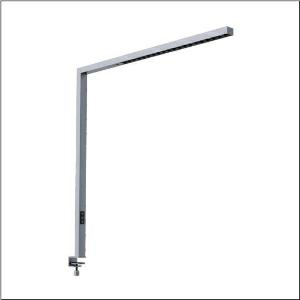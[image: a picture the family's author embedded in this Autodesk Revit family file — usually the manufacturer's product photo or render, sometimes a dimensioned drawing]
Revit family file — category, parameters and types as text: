
# Revit family: silica_r__31_desk_51my52ga3cs_3f63
name_source: partatom
category: Lighting Fixtures
units: mm (PartAtom-declared; Revit-internal decimal feet)

## family parameters
Cut with Voids When Loaded = No
Host = Face
Light Source = No
Part Type = Normal
Room Calculation Point = No
Round Connector Dimension = Use Diameter
Shared = No

## types (1)
- Silica® 31 Desk (1 x LED, 10300 lm, 75 W, 3000K)
    Apparent Load = 75 VA
    CIE Flux Codes = 86 100 100 24 100
    Color Rendering = 80
    Color Temperature = 3000K
    Default Elevation = 1800 mm
    Description = Silica® 31 Desk, desktop luminaire, secondary optical cover: cover panel, of PMMA, light emission: direct/indirect distribution, primary light characteristic: symmetric, installation type: as desk luminaire, LED, rated luminous flux: 10.300lm, luminous efficacy: 137lm/W, light colour: 830, colour temperature: 3000K, control gear: Touchdim, daylight-dependent control, with cable with plug, mains connection: 230V, AC, 50Hz, connection cable pre-assembled, rated input power: 75W, luminaire head, of aluminium, metallic grey (RAL 9006), length: 1.203mm, width: 52mm, supporting column, angular, of aluminium, metallic grey (RAL 9006), baseplate, of steel, metallic grey (RAL 9006), protection rating (complete): IP20, insulation class (complete): insulation class I (protective earthing), certification: CE, permissible operating ambient temperature: -20..+40°C, standard: EN 50419, packaging unit: 1 piece
    Height = 36 mm
    Lamp = 1 x LED
    Lamp Light Flux = 10300 lm
    Lamp Power = 75 W
    Lamp count = 1
    Length = 1203 mm
    Luminous efficacy = 137 lm/W
    Manufacturer = Siteco
    ModVariant = No
    Model = 51MY52GA3CS
    Mounting Place = Floor
    Mounting Type = Freestanding
    Number of Poles = 1
    OnlyDefault = Yes
    Power Factor = 1
    Product Name = Silica® 31 Desk
    Product group = desktop luminaire
    ProductGroupID = 1303
    Protection Class = Protection class I
    Protection Degree = IP 20
    RLX_Detail_Level = 1
    RLX_Emergency_Light_Flux = 0 lm
    RLX_Emergency_Type = 0
    RLX_Emergency_Type_DB = No
    RlxData = <blob elided: 19653 chars, md5=0569b609>
    Socket = socket
    Standby Power = 0 W
    System Light Flux = 10300 lm
    System Power = 75 W
    Type Comments = Product without accessories
    Type Image = l_1275333.jpg
    URL = http://relux.com
    VarID = ---
    Voltage = 0 V
    Weight = 0.00 kg
    Width = 52 mm

## geometry (parser evidence)
native form markers: Blend x4, Sweep x16
no freeform markers — native parametric forms only
